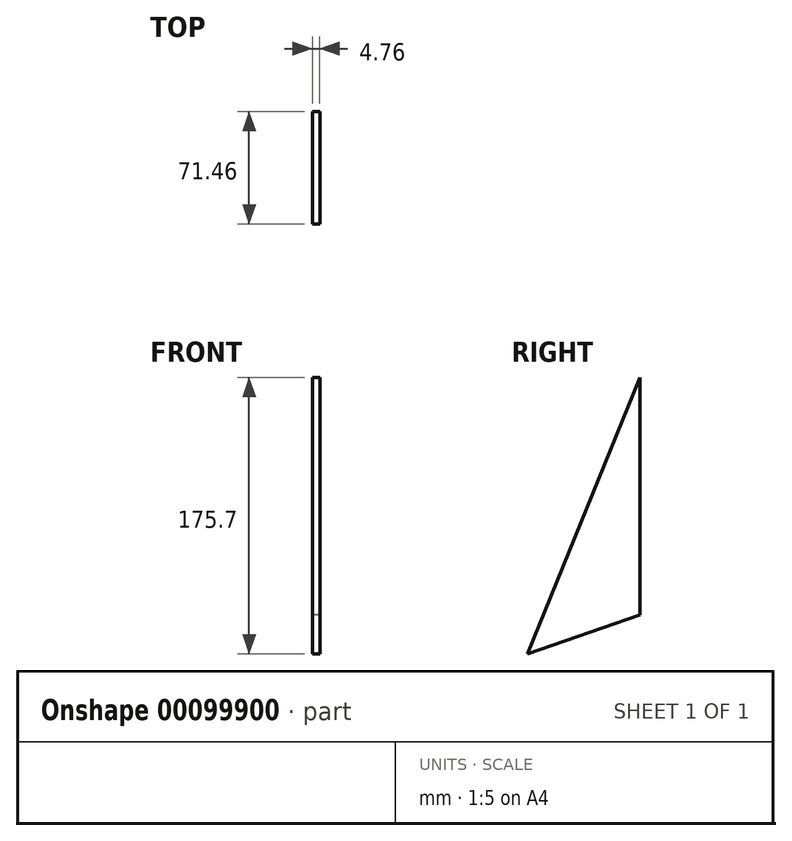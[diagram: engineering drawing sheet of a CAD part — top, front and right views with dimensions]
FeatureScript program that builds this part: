
annotation { "Feature Type Name" : "Feature", "Feature Type Description" : "" }
export const myFeature = defineFeature(function(context is Context, id is Id, definition is map)
    precondition{}
    {
        {
            var Q0;
            Q0=qCreatedBy(makeId("Right.planeOp"),FACE);
            var sketch = newSketch(context, id + "F0", { "sketchPlane" : qUnion([Q0])});
            skLineSegment(sketch, "E0", {"start": v(0, 0) * mm, "end": v(0, 152.4) * mm});
            skPoint(sketch, "E1.end.orphan", {"position": v(-76.2, 0) * mm});
            skLineSegment(sketch, "E2", {"start": v(-72.06, -24.77) * mm, "end": v(0, 152.4) * mm});
            skPoint(sketch, "E3", {"position": v(-71.46, -23.3) * mm});
            skPoint(sketch, "E4", {"position": v(0, 1.59) * mm});
            skLineSegment(sketch, "E5", {"start": v(-71.46, -23.3) * mm, "end": v(0, 1.59) * mm});
            skSolve(sketch);
        }
        {
            var Q0;
            Q0 = qSketchRegion(id + "F0", true);
            extrude(context, id + "F1", {"entities" : qUnion([Q0]), "depth" : 4.76 * mm});
        }
    });
